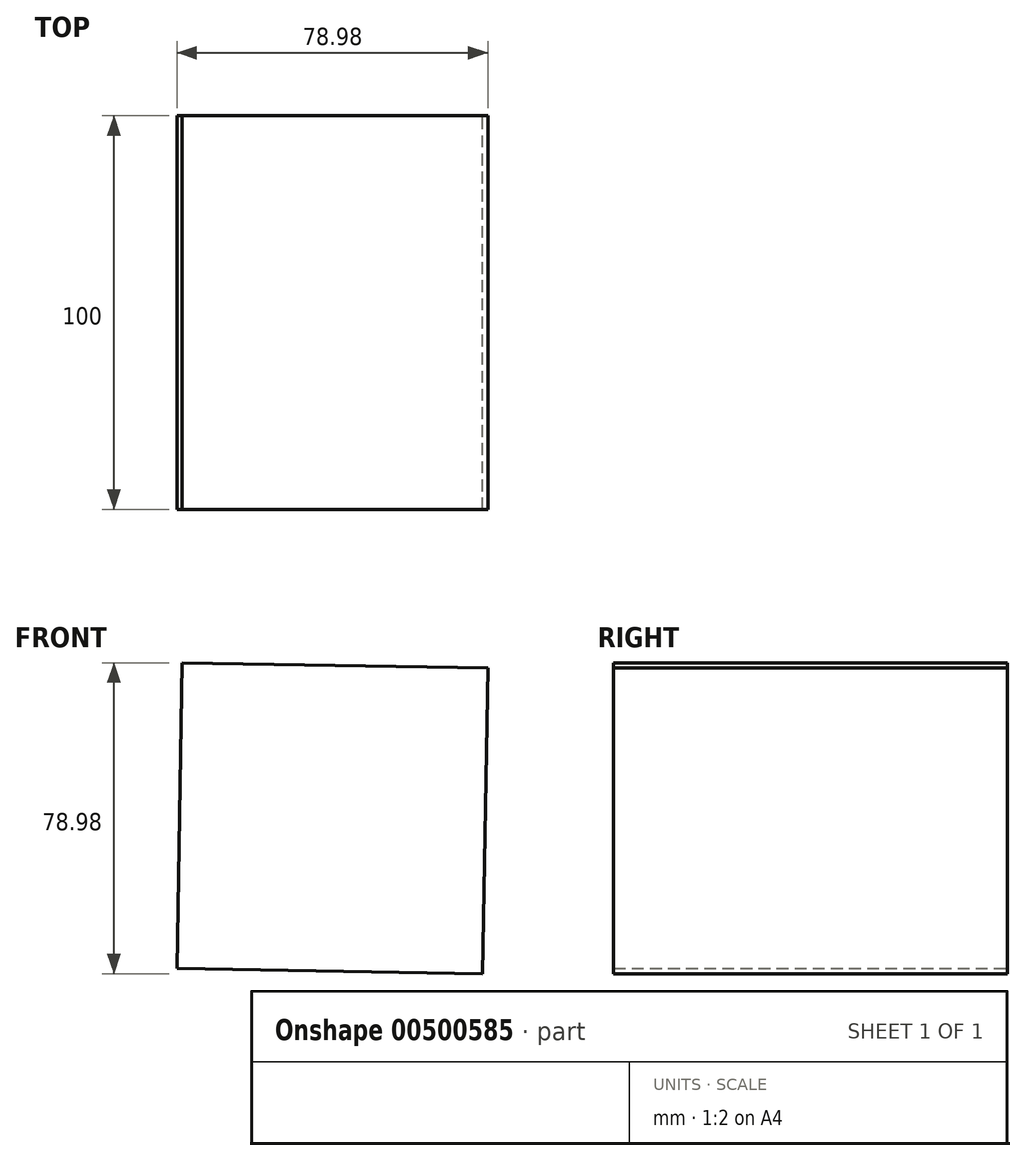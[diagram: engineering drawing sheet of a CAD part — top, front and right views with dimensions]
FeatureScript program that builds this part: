
annotation { "Feature Type Name" : "Feature", "Feature Type Description" : "" }
export const myFeature = defineFeature(function(context is Context, id is Id, definition is map)
    precondition{}
    {
        {
            var Q0;
            Q0=qCreatedBy(makeId("Front.planeOp"),FACE);
            var sketch = newSketch(context, id + "F0", { "sketchPlane" : qUnion([Q0])});
            skCircle(sketch, "E0.cCircle", {"center": v(0, 0) * mm, "radius": 54.93 * mm, "construction": true});
            skLineSegment(sketch, "E0.0", {"start": v(-38.18, 39.5) * mm, "end": v(39.5, 38.18) * mm});
            skLineSegment(sketch, "E0.1", {"start": v(39.5, 38.18) * mm, "end": v(38.18, -39.5) * mm});
            skLineSegment(sketch, "E0.2", {"start": v(38.18, -39.5) * mm, "end": v(-39.5, -38.18) * mm});
            skLineSegment(sketch, "E0.3", {"start": v(-39.5, -38.18) * mm, "end": v(-38.18, 39.5) * mm});
            skSolve(sketch);
        }
        {
            var Q0;
            Q0=makeQuery(id+"F0.imprint","IMPRINT",FACE,{"disambiguationData":[TD([[makeQuery(id+"F0.imprint","IMPRINT",EDGE,{"derivedFrom":sQuery(id+"F0.wireOp",EDGE,"E0.0")}),-1.0]])]});
            extrude(context, id + "F1", {"entities" : qUnion([Q0]), "endBound" : BoundingType.SYMMETRIC, "depth" : 100 * mm});
        }
    });
